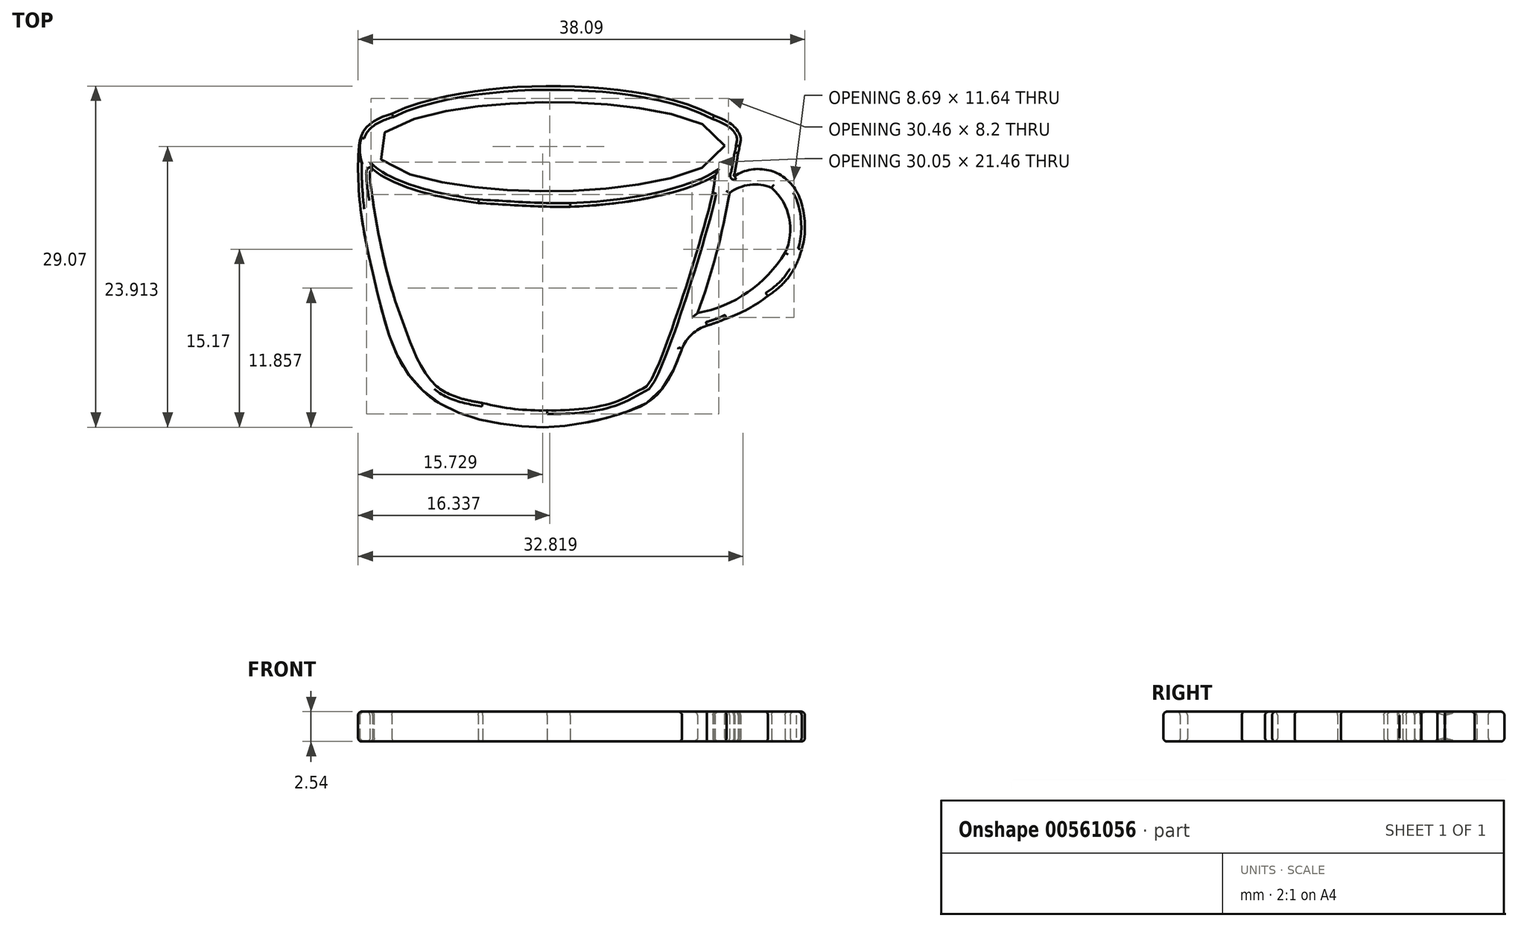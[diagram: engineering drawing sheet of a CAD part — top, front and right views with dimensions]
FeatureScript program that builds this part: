
annotation { "Feature Type Name" : "Feature", "Feature Type Description" : "" }
export const myFeature = defineFeature(function(context is Context, id is Id, definition is map)
    precondition{}
    {
        {
            var Q0;
            Q0=qCreatedBy(makeId("Top.planeOp"),FACE);
            var sketch = newSketch(context, id + "F0", { "sketchPlane" : qUnion([Q0])});
            skPoint(sketch, "E0.middle", {"position": v(0, 0) * mm});
            skFitSpline(sketch, "E1", {"points": [v(-17.37, 10.42) * mm, v(-18.4, 9.54) * mm, v(-18.84, 8.07) * mm, v(-18.7, 2.77) * mm, v(-17.37, -3.85) * mm, v(-15.46, -9.88) * mm, v(-12.66, -13.27) * mm, v(-8.84, -15.03) * mm, v(-2.8, -15.77) * mm, v(2.05, -15.03) * mm, v(5.14, -14) * mm, v(6.61, -12.97) * mm, v(8.23, -10.32) * mm, v(9.56, -7.23) * mm, v(10, -7.23) * mm, v(12.5, -6.5) * mm, v(16.03, -4.58) * mm, v(17.98, -2.72) * mm, v(19.06, 0) * mm, v(19.13, 2.14) * mm, v(18.45, 4.36) * mm, v(16.9, 5.78) * mm, v(15.08, 6.05) * mm, v(13.53, 5.78) * mm, v(13.2, 5.64) * mm, v(13.13, 5.64) * mm, v(13.2, 5.91) * mm, v(13.6, 8.22) * mm, v(13.72, 8.82) * mm, v(13.04, 9.95) * mm, v(8.39, 11.54) * mm, v(3.17, 12.1) * mm, v(-1.48, 12.34) * mm, v(-6.02, 12.22) * mm, v(-10.79, 11.88) * mm, v(-15.55, 11.09) * mm, v(-17.37, 10.42) * mm]});
            skFitSpline(sketch, "E2", {"points": [v(-17.81, 6.12) * mm, v(-15.16, 4.5) * mm, v(-8.4, 3.32) * mm, v(-2.8, 3.03) * mm, v(2.64, 3.17) * mm, v(7.94, 4.06) * mm, v(11.17, 5.13) * mm, v(11.32, 4.2) * mm, v(6.02, -11.84) * mm, v(5.14, -12.57) * mm, v(3.08, -13.6) * mm, v(-2.8, -14.34) * mm, v(-8.1, -13.75) * mm, v(-12.22, -12.28) * mm, v(-14.72, -7.86) * mm, v(-16.49, -2.42) * mm, v(-17.66, 3.61) * mm, v(-17.9, 5.43) * mm, v(-17.9, 5.87) * mm, v(-17.81, 6.12) * mm]});
            skEllipse(sketch, "E3", {"center": v(-2.58, 8.14) * mm, "majorRadius": 14.93 * mm, "minorRadius": 3.8 * mm, "majorAxis": v(1, 0)});
            skEllipticalArc(sketch, "E4", {});
            skArc(sketch, "E5", {"start": v(-18.76, 8.3) * mm, "mid": v(-18.86, 5.53) * mm, "end": v(-18.7, 2.77) * mm});
            skArc(sketch, "E6", {"start": v(11.32, 4.2) * mm, "mid": v(11.45, 4.93) * mm, "end": v(11.52, 5.67) * mm});
            skEllipticalArc(sketch, "E7.trimOffspring", {});
            skEllipticalArc(sketch, "E8.trimOffspring", {});
            skArc(sketch, "E9", {"start": v(-17.66, 6.2) * mm, "mid": v(-17.74, 4.9) * mm, "end": v(-17.66, 3.61) * mm});
            skArc(sketch, "E10", {"start": v(-12.22, -12.28) * mm, "mid": v(-3.27, -14.34) * mm, "end": v(5.69, -12.28) * mm});
            skFitSpline(sketch, "E11.trimOffspring", {"points": [v(-17.81, 6.12) * mm, v(-15.16, 4.5) * mm, v(-8.4, 3.32) * mm, v(-2.8, 3.03) * mm, v(2.64, 3.17) * mm, v(7.94, 4.06) * mm, v(11.17, 5.13) * mm, v(11.32, 4.2) * mm, v(6.02, -11.84) * mm, v(5.14, -12.57) * mm, v(3.08, -13.6) * mm, v(-2.8, -14.34) * mm, v(-8.1, -13.75) * mm, v(-12.22, -12.28) * mm, v(-14.72, -7.86) * mm, v(-16.49, -2.42) * mm, v(-17.66, 3.61) * mm, v(-17.9, 5.43) * mm, v(-17.9, 5.87) * mm, v(-17.81, 6.12) * mm]});
            skArc(sketch, "E12", {"start": v(10.97, -7.07) * mm, "mid": v(9.54, -7.85) * mm, "end": v(8.66, -9.22) * mm});
            skArc(sketch, "E13", {"start": v(18.45, 4.36) * mm, "mid": v(16.1, 6.13) * mm, "end": v(13.2, 5.64) * mm});
            skArc(sketch, "E14", {"start": v(17.98, -2.72) * mm, "mid": v(19.14, 0.76) * mm, "end": v(18.45, 4.36) * mm});
            skArc(sketch, "E15", {"start": v(12.5, -6.5) * mm, "mid": v(15.5, -4.98) * mm, "end": v(17.98, -2.72) * mm});
            skArc(sketch, "E16", {"start": v(16.34, 4.63) * mm, "mid": v(14.5, 4.9) * mm, "end": v(12.76, 4.2) * mm});
            skArc(sketch, "E17", {"start": v(17.49, -0.9) * mm, "mid": v(17.85, 2.05) * mm, "end": v(16.34, 4.63) * mm});
            skArc(sketch, "E18", {"start": v(10.03, -6.04) * mm, "mid": v(14.31, -4.27) * mm, "end": v(17.49, -0.9) * mm});
            skPoint(sketch, "E19.orphan", {"position": v(12.88, 4.63) * mm});
            skArc(sketch, "E20", {"start": v(10.03, -6.04) * mm, "mid": v(11.63, -0.98) * mm, "end": v(12.76, 4.2) * mm});
            const initialGuessF0  = {"E4": [-0.002582713961602469, 0.008142811246206635, 0.9999896746917578, 0.0045442832077832295, 0.016189123954817964, 0.0051608500665675395, 4.81986095342071, 5.768963313134002], "E7.trimOffspring": [-0.002582713961602469, 0.008142811246206635, 0.9999896746917578, 0.0045442832077832295, 0.016189123954817964, 0.0051608500665675395, 6.1611266414338335, 3.127793110283517], "E8.trimOffspring": [-0.002582713961602469, 0.008142811246206635, 0.9999896746917578, 0.0045442832077832295, 0.016189123954817964, 0.0051608500665675395, 3.5120995657733793, 4.326554214382226]};
            skSetInitialGuess(sketch, initialGuessF0);
            skSolve(sketch);
        }
        {
            var Q0;
            Q0 = qSketchRegion(id + "F0", true);
            extrude(context, id + "F1", {"entities" : qUnion([Q0]), "depth" : 2.54 * mm, "offsetDistance" : 25.4 * mm});
        }
        {
            var Q0;
            Q0=makeQuery(id+"F1.opExtrude","CAP_FACE",FACE,{"disambiguationData":[OSD([sQuery(id+"F0.wireOp",EDGE,"E1"),sQuery(id+"F0.wireOp",EDGE,"E2"),sQuery(id+"F0.wireOp",EDGE,"E3"),sQuery(id+"F0.wireOp",EDGE,"E4"),sQuery(id+"F0.wireOp",EDGE,"E5"),sQuery(id+"F0.wireOp",EDGE,"E6"),sQuery(id+"F0.wireOp",EDGE,"E2"),sQuery(id+"F0.wireOp",EDGE,"E7.trimOffspring"),sQuery(id+"F0.wireOp",EDGE,"E8.trimOffspring"),sQuery(id+"F0.wireOp",EDGE,"E9"),sQuery(id+"F0.wireOp",EDGE,"E10"),sQuery(id+"F0.wireOp",EDGE,"E11.trimOffspring"),sQuery(id+"F0.wireOp",EDGE,"E12"),sQuery(id+"F0.wireOp",EDGE,"E1"),sQuery(id+"F0.wireOp",EDGE,"E13"),sQuery(id+"F0.wireOp",EDGE,"E1"),sQuery(id+"F0.wireOp",EDGE,"E14"),sQuery(id+"F0.wireOp",EDGE,"E15"),sQuery(id+"F0.wireOp",EDGE,"E1"),sQuery(id+"F0.wireOp",EDGE,"E16"),sQuery(id+"F0.wireOp",EDGE,"E17"),sQuery(id+"F0.wireOp",EDGE,"E18"),sQuery(id+"F0.wireOp",EDGE,"E20")])],"isStart":false});
            var Q1;
            Q1=makeQuery(id+"F1.opExtrude","CAP_FACE",FACE,{"disambiguationData":[OSD([sQuery(id+"F0.wireOp",EDGE,"E1"),sQuery(id+"F0.wireOp",EDGE,"E2"),sQuery(id+"F0.wireOp",EDGE,"E3"),sQuery(id+"F0.wireOp",EDGE,"E4"),sQuery(id+"F0.wireOp",EDGE,"E5"),sQuery(id+"F0.wireOp",EDGE,"E6"),sQuery(id+"F0.wireOp",EDGE,"E2"),sQuery(id+"F0.wireOp",EDGE,"E7.trimOffspring"),sQuery(id+"F0.wireOp",EDGE,"E8.trimOffspring"),sQuery(id+"F0.wireOp",EDGE,"E9"),sQuery(id+"F0.wireOp",EDGE,"E10"),sQuery(id+"F0.wireOp",EDGE,"E11.trimOffspring"),sQuery(id+"F0.wireOp",EDGE,"E12"),sQuery(id+"F0.wireOp",EDGE,"E1"),sQuery(id+"F0.wireOp",EDGE,"E13"),sQuery(id+"F0.wireOp",EDGE,"E1"),sQuery(id+"F0.wireOp",EDGE,"E14"),sQuery(id+"F0.wireOp",EDGE,"E15"),sQuery(id+"F0.wireOp",EDGE,"E1"),sQuery(id+"F0.wireOp",EDGE,"E16"),sQuery(id+"F0.wireOp",EDGE,"E17"),sQuery(id+"F0.wireOp",EDGE,"E18"),sQuery(id+"F0.wireOp",EDGE,"E20")])],"isStart":true});
            fillet(context, id + "F2", {"entities" : qUnion([Q0, Q1]), "radius" : 0.3 * mm, "tangentPropagation" : true, "allowEdgeOverflow" : false});
        }
    });
